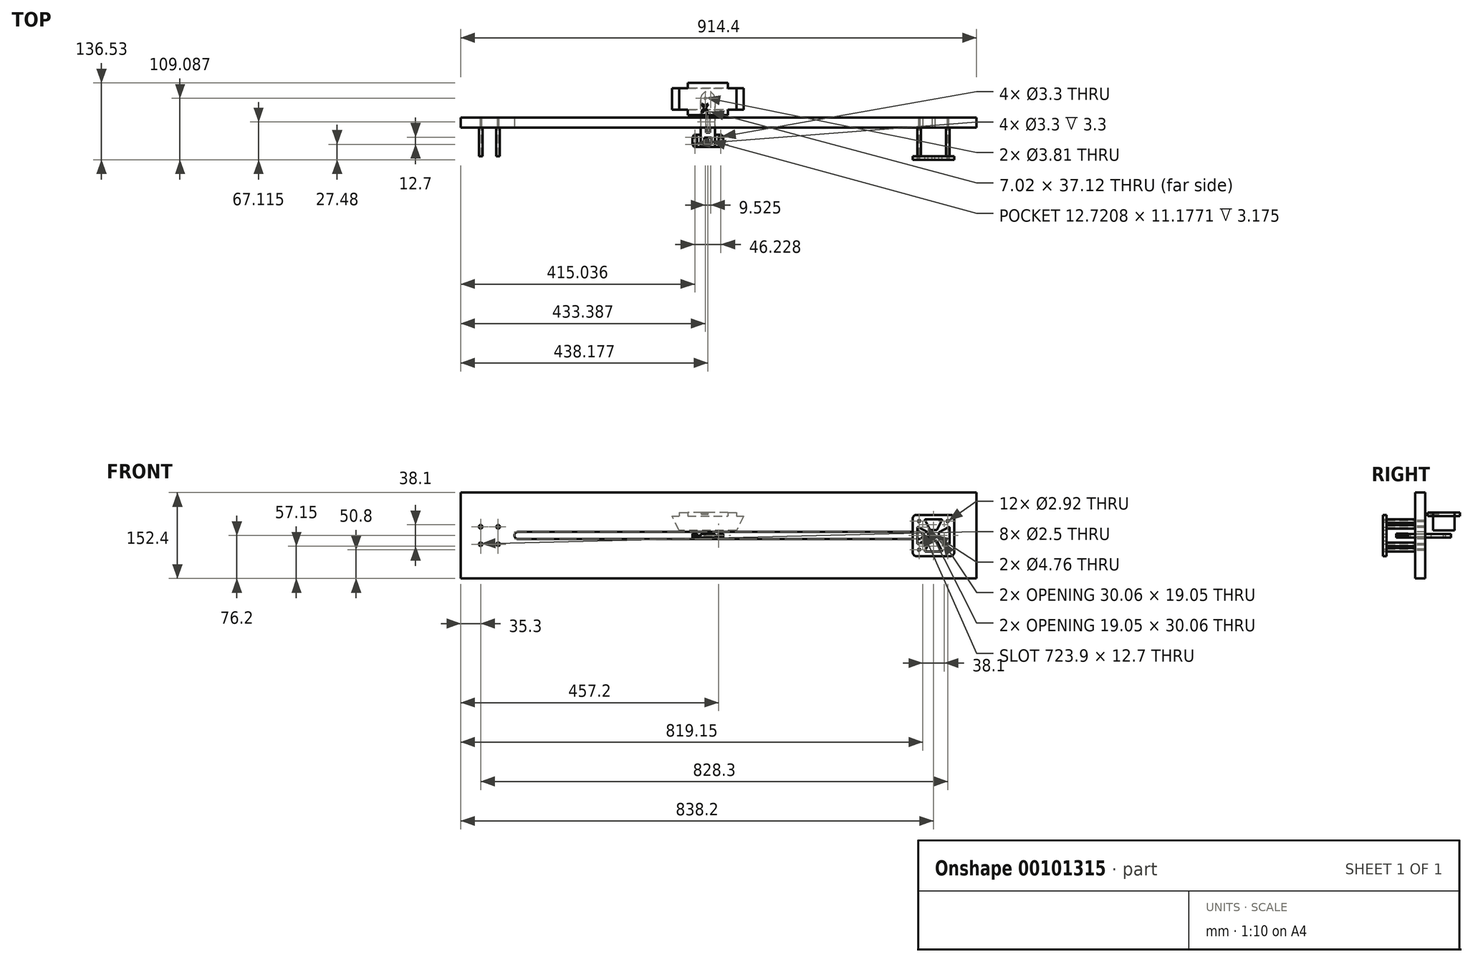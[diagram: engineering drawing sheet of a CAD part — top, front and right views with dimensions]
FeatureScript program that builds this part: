
annotation { "Feature Type Name" : "Feature", "Feature Type Description" : "" }
export const myFeature = defineFeature(function(context is Context, id is Id, definition is map)
    precondition{}
    {
        {
            var Q0;
            Q0=qCreatedBy(makeId("Front.planeOp"),FACE);
            var sketch = newSketch(context, id + "F0", { "sketchPlane" : qUnion([Q0])});
            skLineSegment(sketch, "E0", {"start": v(0, 0) * mm, "end": v(0.2, 0) * mm});
            skArc(sketch, "E1", {"start": v(0.2, 0) * mm, "mid": v(0.29, 0.02) * mm, "end": v(0.34, 0.09) * mm});
            skLineSegment(sketch, "E2", {"start": v(0.75, 0.76) * mm, "end": v(1.25, 0.76) * mm});
            skArc(sketch, "E3", {"start": v(1.66, 0.09) * mm, "mid": v(1.71, 0.02) * mm, "end": v(1.8, 0) * mm});
            skLineSegment(sketch, "E4", {"start": v(1.8, 0) * mm, "end": v(2, 0) * mm});
            skLineSegment(sketch, "E5", {"start": v(0.34, 0.09) * mm, "end": v(0.61, 0.67) * mm});
            skLineSegment(sketch, "E6", {"start": v(1.66, 0.09) * mm, "end": v(1.39, 0.67) * mm});
            skArc(sketch, "E7", {"start": v(1.39, 0.67) * mm, "mid": v(1.33, 0.74) * mm, "end": v(1.25, 0.76) * mm});
            skArc(sketch, "E8", {"start": v(0.61, 0.67) * mm, "mid": v(0.67, 0.74) * mm, "end": v(0.75, 0.76) * mm});
            skLineSegment(sketch, "E9.1.0.0", {"start": v(2, 0) * mm, "end": v(2.2, 0) * mm});
            skArc(sketch, "E9.1.0.1", {"start": v(2.2, 0) * mm, "mid": v(2.29, 0.02) * mm, "end": v(2.34, 0.09) * mm});
            skLineSegment(sketch, "E9.1.0.2", {"start": v(2.34, 0.09) * mm, "end": v(2.61, 0.67) * mm});
            skArc(sketch, "E9.1.0.3", {"start": v(2.61, 0.67) * mm, "mid": v(2.67, 0.74) * mm, "end": v(2.75, 0.76) * mm});
            skLineSegment(sketch, "E9.1.0.4", {"start": v(2.75, 0.76) * mm, "end": v(3.25, 0.76) * mm});
            skArc(sketch, "E9.1.0.5", {"start": v(3.39, 0.67) * mm, "mid": v(3.33, 0.74) * mm, "end": v(3.25, 0.76) * mm});
            skLineSegment(sketch, "E9.1.0.6", {"start": v(3.66, 0.09) * mm, "end": v(3.39, 0.67) * mm});
            skArc(sketch, "E9.1.0.7", {"start": v(3.66, 0.09) * mm, "mid": v(3.71, 0.02) * mm, "end": v(3.8, 0) * mm});
            skLineSegment(sketch, "E9.1.0.8", {"start": v(3.8, 0) * mm, "end": v(4, 0) * mm});
            skLineSegment(sketch, "E9.2.0.0", {"start": v(4, 0) * mm, "end": v(4.2, 0) * mm});
            skArc(sketch, "E9.2.0.1", {"start": v(4.2, 0) * mm, "mid": v(4.29, 0.02) * mm, "end": v(4.34, 0.09) * mm});
            skLineSegment(sketch, "E9.2.0.2", {"start": v(4.34, 0.09) * mm, "end": v(4.61, 0.67) * mm});
            skArc(sketch, "E9.2.0.3", {"start": v(4.61, 0.67) * mm, "mid": v(4.67, 0.74) * mm, "end": v(4.75, 0.76) * mm});
            skLineSegment(sketch, "E9.2.0.4", {"start": v(4.75, 0.76) * mm, "end": v(5.25, 0.76) * mm});
            skArc(sketch, "E9.2.0.5", {"start": v(5.39, 0.67) * mm, "mid": v(5.33, 0.74) * mm, "end": v(5.25, 0.76) * mm});
            skLineSegment(sketch, "E9.2.0.6", {"start": v(5.66, 0.09) * mm, "end": v(5.39, 0.67) * mm});
            skArc(sketch, "E9.2.0.7", {"start": v(5.66, 0.09) * mm, "mid": v(5.71, 0.02) * mm, "end": v(5.8, 0) * mm});
            skLineSegment(sketch, "E9.2.0.8", {"start": v(5.8, 0) * mm, "end": v(6, 0) * mm});
            skLineSegment(sketch, "E9.3.0.0", {"start": v(6, 0) * mm, "end": v(6.2, 0) * mm});
            skArc(sketch, "E9.3.0.1", {"start": v(6.2, 0) * mm, "mid": v(6.29, 0.02) * mm, "end": v(6.34, 0.09) * mm});
            skLineSegment(sketch, "E9.3.0.2", {"start": v(6.34, 0.09) * mm, "end": v(6.61, 0.67) * mm});
            skArc(sketch, "E9.3.0.3", {"start": v(6.61, 0.67) * mm, "mid": v(6.67, 0.74) * mm, "end": v(6.75, 0.76) * mm});
            skLineSegment(sketch, "E9.3.0.4", {"start": v(6.75, 0.76) * mm, "end": v(7.25, 0.76) * mm});
            skArc(sketch, "E9.3.0.5", {"start": v(7.39, 0.67) * mm, "mid": v(7.33, 0.74) * mm, "end": v(7.25, 0.76) * mm});
            skLineSegment(sketch, "E9.3.0.6", {"start": v(7.66, 0.09) * mm, "end": v(7.39, 0.67) * mm});
            skArc(sketch, "E9.3.0.7", {"start": v(7.66, 0.09) * mm, "mid": v(7.71, 0.02) * mm, "end": v(7.8, 0) * mm});
            skLineSegment(sketch, "E9.3.0.8", {"start": v(7.8, 0) * mm, "end": v(8, 0) * mm});
            skLineSegment(sketch, "E9.4.0.0", {"start": v(8, 0) * mm, "end": v(8.2, 0) * mm});
            skArc(sketch, "E9.4.0.1", {"start": v(8.2, 0) * mm, "mid": v(8.29, 0.02) * mm, "end": v(8.34, 0.09) * mm});
            skLineSegment(sketch, "E9.4.0.2", {"start": v(8.34, 0.09) * mm, "end": v(8.61, 0.67) * mm});
            skArc(sketch, "E9.4.0.3", {"start": v(8.61, 0.67) * mm, "mid": v(8.67, 0.74) * mm, "end": v(8.75, 0.76) * mm});
            skLineSegment(sketch, "E9.4.0.4", {"start": v(8.75, 0.76) * mm, "end": v(9.25, 0.76) * mm});
            skArc(sketch, "E9.4.0.5", {"start": v(9.39, 0.67) * mm, "mid": v(9.33, 0.74) * mm, "end": v(9.25, 0.76) * mm});
            skLineSegment(sketch, "E9.4.0.6", {"start": v(9.66, 0.09) * mm, "end": v(9.39, 0.67) * mm});
            skArc(sketch, "E9.4.0.7", {"start": v(9.66, 0.09) * mm, "mid": v(9.71, 0.02) * mm, "end": v(9.8, 0) * mm});
            skLineSegment(sketch, "E9.4.0.8", {"start": v(9.8, 0) * mm, "end": v(10, 0) * mm});
            skLineSegment(sketch, "E9.5.0.0", {"start": v(10, 0) * mm, "end": v(10.2, 0) * mm});
            skArc(sketch, "E9.5.0.1", {"start": v(10.2, 0) * mm, "mid": v(10.29, 0.02) * mm, "end": v(10.34, 0.09) * mm});
            skLineSegment(sketch, "E9.5.0.2", {"start": v(10.34, 0.09) * mm, "end": v(10.61, 0.67) * mm});
            skArc(sketch, "E9.5.0.3", {"start": v(10.61, 0.67) * mm, "mid": v(10.67, 0.74) * mm, "end": v(10.75, 0.76) * mm});
            skLineSegment(sketch, "E9.5.0.4", {"start": v(10.75, 0.76) * mm, "end": v(11.25, 0.76) * mm});
            skArc(sketch, "E9.5.0.5", {"start": v(11.39, 0.67) * mm, "mid": v(11.33, 0.74) * mm, "end": v(11.25, 0.76) * mm});
            skLineSegment(sketch, "E9.5.0.6", {"start": v(11.66, 0.09) * mm, "end": v(11.39, 0.67) * mm});
            skArc(sketch, "E9.5.0.7", {"start": v(11.66, 0.09) * mm, "mid": v(11.71, 0.02) * mm, "end": v(11.8, 0) * mm});
            skLineSegment(sketch, "E9.5.0.8", {"start": v(11.8, 0) * mm, "end": v(12, 0) * mm});
            skLineSegment(sketch, "E9.6.0.0", {"start": v(12, 0) * mm, "end": v(12.2, 0) * mm});
            skArc(sketch, "E9.6.0.1", {"start": v(12.2, 0) * mm, "mid": v(12.29, 0.02) * mm, "end": v(12.34, 0.09) * mm});
            skLineSegment(sketch, "E9.6.0.2", {"start": v(12.34, 0.09) * mm, "end": v(12.61, 0.67) * mm});
            skArc(sketch, "E9.6.0.3", {"start": v(12.61, 0.67) * mm, "mid": v(12.67, 0.74) * mm, "end": v(12.75, 0.76) * mm});
            skLineSegment(sketch, "E9.6.0.4", {"start": v(12.75, 0.76) * mm, "end": v(13.25, 0.76) * mm});
            skArc(sketch, "E9.6.0.5", {"start": v(13.39, 0.67) * mm, "mid": v(13.33, 0.74) * mm, "end": v(13.25, 0.76) * mm});
            skLineSegment(sketch, "E9.6.0.6", {"start": v(13.66, 0.09) * mm, "end": v(13.39, 0.67) * mm});
            skArc(sketch, "E9.6.0.7", {"start": v(13.66, 0.09) * mm, "mid": v(13.71, 0.02) * mm, "end": v(13.8, 0) * mm});
            skLineSegment(sketch, "E9.6.0.8", {"start": v(13.8, 0) * mm, "end": v(14, 0) * mm});
            skLineSegment(sketch, "E9.7.0.0", {"start": v(14, 0) * mm, "end": v(14.2, 0) * mm});
            skArc(sketch, "E9.7.0.1", {"start": v(14.2, 0) * mm, "mid": v(14.29, 0.02) * mm, "end": v(14.34, 0.09) * mm});
            skLineSegment(sketch, "E9.7.0.2", {"start": v(14.34, 0.09) * mm, "end": v(14.61, 0.67) * mm});
            skArc(sketch, "E9.7.0.3", {"start": v(14.61, 0.67) * mm, "mid": v(14.67, 0.74) * mm, "end": v(14.75, 0.76) * mm});
            skLineSegment(sketch, "E9.7.0.4", {"start": v(14.75, 0.76) * mm, "end": v(15.25, 0.76) * mm});
            skArc(sketch, "E9.7.0.5", {"start": v(15.39, 0.67) * mm, "mid": v(15.33, 0.74) * mm, "end": v(15.25, 0.76) * mm});
            skLineSegment(sketch, "E9.7.0.6", {"start": v(15.66, 0.09) * mm, "end": v(15.39, 0.67) * mm});
            skArc(sketch, "E9.7.0.7", {"start": v(15.66, 0.09) * mm, "mid": v(15.71, 0.02) * mm, "end": v(15.8, 0) * mm});
            skLineSegment(sketch, "E9.7.0.8", {"start": v(15.8, 0) * mm, "end": v(16, 0) * mm});
            skLineSegment(sketch, "E9.direction1", {"start": v(0, 0) * mm, "end": v(2, 0) * mm, "construction": true});
            skLineSegment(sketch, "E10", {"start": v(0, 0) * mm, "end": v(0, -0.76) * mm});
            skLineSegment(sketch, "E11", {"start": v(0, -0.76) * mm, "end": v(16, -0.76) * mm});
            skLineSegment(sketch, "E12", {"start": v(16, -0.76) * mm, "end": v(16, 0) * mm});
            skSolve(sketch);
        }
        {
            var Q0;
            Q0=makeQuery(id+"F0.imprint","IMPRINT",FACE,{"disambiguationData":[TD([[makeQuery(id+"F0.imprint","IMPRINT",EDGE,{"derivedFrom":sQuery(id+"F0.wireOp",EDGE,"E0")}),-1.0]])]});
            extrude(context, id + "F1", {"entities" : qUnion([Q0]), "depth" : 6 * mm});
        }
        {
            var Q0;
            Q0=makeQuery(id+"F1.opExtrude","CAP_FACE",FACE,{"disambiguationData":[OSD([sQuery(id+"F0.wireOp",EDGE,"E0"),sQuery(id+"F0.wireOp",EDGE,"E1"),sQuery(id+"F0.wireOp",EDGE,"E2"),sQuery(id+"F0.wireOp",EDGE,"E3"),sQuery(id+"F0.wireOp",EDGE,"E4"),sQuery(id+"F0.wireOp",EDGE,"E5"),sQuery(id+"F0.wireOp",EDGE,"E6"),sQuery(id+"F0.wireOp",EDGE,"E7"),sQuery(id+"F0.wireOp",EDGE,"E8"),sQuery(id+"F0.wireOp",EDGE,"E9.1.0.0"),sQuery(id+"F0.wireOp",EDGE,"E9.1.0.1"),sQuery(id+"F0.wireOp",EDGE,"E9.1.0.2"),sQuery(id+"F0.wireOp",EDGE,"E9.1.0.3"),sQuery(id+"F0.wireOp",EDGE,"E9.1.0.4"),sQuery(id+"F0.wireOp",EDGE,"E9.1.0.5"),sQuery(id+"F0.wireOp",EDGE,"E9.1.0.6"),sQuery(id+"F0.wireOp",EDGE,"E9.1.0.7"),sQuery(id+"F0.wireOp",EDGE,"E9.1.0.8"),sQuery(id+"F0.wireOp",EDGE,"E9.2.0.0"),sQuery(id+"F0.wireOp",EDGE,"E9.2.0.1"),sQuery(id+"F0.wireOp",EDGE,"E9.2.0.2"),sQuery(id+"F0.wireOp",EDGE,"E9.2.0.3"),sQuery(id+"F0.wireOp",EDGE,"E9.2.0.4"),sQuery(id+"F0.wireOp",EDGE,"E9.2.0.5"),sQuery(id+"F0.wireOp",EDGE,"E9.2.0.6"),sQuery(id+"F0.wireOp",EDGE,"E9.2.0.7"),sQuery(id+"F0.wireOp",EDGE,"E9.2.0.8"),sQuery(id+"F0.wireOp",EDGE,"E9.3.0.0"),sQuery(id+"F0.wireOp",EDGE,"E9.3.0.1"),sQuery(id+"F0.wireOp",EDGE,"E9.3.0.2"),sQuery(id+"F0.wireOp",EDGE,"E9.3.0.3"),sQuery(id+"F0.wireOp",EDGE,"E9.3.0.4"),sQuery(id+"F0.wireOp",EDGE,"E9.3.0.5"),sQuery(id+"F0.wireOp",EDGE,"E9.3.0.6"),sQuery(id+"F0.wireOp",EDGE,"E9.3.0.7"),sQuery(id+"F0.wireOp",EDGE,"E9.3.0.8"),sQuery(id+"F0.wireOp",EDGE,"E9.4.0.0"),sQuery(id+"F0.wireOp",EDGE,"E9.4.0.1"),sQuery(id+"F0.wireOp",EDGE,"E9.4.0.2"),sQuery(id+"F0.wireOp",EDGE,"E9.4.0.3"),sQuery(id+"F0.wireOp",EDGE,"E9.4.0.4"),sQuery(id+"F0.wireOp",EDGE,"E9.4.0.5"),sQuery(id+"F0.wireOp",EDGE,"E9.4.0.6"),sQuery(id+"F0.wireOp",EDGE,"E9.4.0.7"),sQuery(id+"F0.wireOp",EDGE,"E9.4.0.8"),sQuery(id+"F0.wireOp",EDGE,"E9.5.0.0"),sQuery(id+"F0.wireOp",EDGE,"E9.5.0.1"),sQuery(id+"F0.wireOp",EDGE,"E9.5.0.2"),sQuery(id+"F0.wireOp",EDGE,"E9.5.0.3"),sQuery(id+"F0.wireOp",EDGE,"E9.5.0.4"),sQuery(id+"F0.wireOp",EDGE,"E9.5.0.5"),sQuery(id+"F0.wireOp",EDGE,"E9.5.0.6"),sQuery(id+"F0.wireOp",EDGE,"E9.5.0.7"),sQuery(id+"F0.wireOp",EDGE,"E9.5.0.8"),sQuery(id+"F0.wireOp",EDGE,"E9.6.0.0"),sQuery(id+"F0.wireOp",EDGE,"E9.6.0.1"),sQuery(id+"F0.wireOp",EDGE,"E9.6.0.2"),sQuery(id+"F0.wireOp",EDGE,"E9.6.0.3"),sQuery(id+"F0.wireOp",EDGE,"E9.6.0.4"),sQuery(id+"F0.wireOp",EDGE,"E9.6.0.5"),sQuery(id+"F0.wireOp",EDGE,"E9.6.0.6"),sQuery(id+"F0.wireOp",EDGE,"E9.6.0.7"),sQuery(id+"F0.wireOp",EDGE,"E9.6.0.8"),sQuery(id+"F0.wireOp",EDGE,"E9.7.0.0"),sQuery(id+"F0.wireOp",EDGE,"E9.7.0.1"),sQuery(id+"F0.wireOp",EDGE,"E9.7.0.2"),sQuery(id+"F0.wireOp",EDGE,"E9.7.0.3"),sQuery(id+"F0.wireOp",EDGE,"E9.7.0.4"),sQuery(id+"F0.wireOp",EDGE,"E9.7.0.5"),sQuery(id+"F0.wireOp",EDGE,"E9.7.0.6"),sQuery(id+"F0.wireOp",EDGE,"E9.7.0.7"),sQuery(id+"F0.wireOp",EDGE,"E9.7.0.8"),sQuery(id+"F0.wireOp",EDGE,"E10"),sQuery(id+"F0.wireOp",EDGE,"E11"),sQuery(id+"F0.wireOp",EDGE,"E12")])],"isStart":false});
            var sketch = newSketch(context, id + "F2", { "sketchPlane" : qUnion([Q0])});
            skLineSegment(sketch, "E13.bottom", {"start": v(0, -3.94) * mm, "end": v(8, -3.94) * mm});
            skLineSegment(sketch, "E13.top", {"start": v(0, 3.3) * mm, "end": v(8, 3.3) * mm});
            skLineSegment(sketch, "E13.left", {"start": v(0, -3.94) * mm, "end": v(0, 3.3) * mm});
            skLineSegment(sketch, "E13.right", {"start": v(8, -3.94) * mm, "end": v(8, 3.3) * mm});
            skPoint(sketch, "E14", {"position": v(8, 0) * mm});
            skSolve(sketch);
        }
        {
            var Q0;
            Q0 = qSketchRegion(id + "F2", true);
            extrude(context, id + "F3", {"entities" : qUnion([Q0]), "oppositeDirection" : true, "depth" : 6 * mm});
        }
        {
            var Q0;
            Q0=makeQuery(id+"F1.opExtrude","SWEPT_BODY",BODY,{"disambiguationData":[OSD([sQuery(id+"F0.wireOp",EDGE,"E0"),sQuery(id+"F0.wireOp",EDGE,"E1"),sQuery(id+"F0.wireOp",EDGE,"E2"),sQuery(id+"F0.wireOp",EDGE,"E3"),sQuery(id+"F0.wireOp",EDGE,"E4"),sQuery(id+"F0.wireOp",EDGE,"E5"),sQuery(id+"F0.wireOp",EDGE,"E6"),sQuery(id+"F0.wireOp",EDGE,"E7"),sQuery(id+"F0.wireOp",EDGE,"E8"),sQuery(id+"F0.wireOp",EDGE,"E9.1.0.0"),sQuery(id+"F0.wireOp",EDGE,"E9.1.0.1"),sQuery(id+"F0.wireOp",EDGE,"E9.1.0.2"),sQuery(id+"F0.wireOp",EDGE,"E9.1.0.3"),sQuery(id+"F0.wireOp",EDGE,"E9.1.0.4"),sQuery(id+"F0.wireOp",EDGE,"E9.1.0.5"),sQuery(id+"F0.wireOp",EDGE,"E9.1.0.6"),sQuery(id+"F0.wireOp",EDGE,"E9.1.0.7"),sQuery(id+"F0.wireOp",EDGE,"E9.1.0.8"),sQuery(id+"F0.wireOp",EDGE,"E9.2.0.0"),sQuery(id+"F0.wireOp",EDGE,"E9.2.0.1"),sQuery(id+"F0.wireOp",EDGE,"E9.2.0.2"),sQuery(id+"F0.wireOp",EDGE,"E9.2.0.3"),sQuery(id+"F0.wireOp",EDGE,"E9.2.0.4"),sQuery(id+"F0.wireOp",EDGE,"E9.2.0.5"),sQuery(id+"F0.wireOp",EDGE,"E9.2.0.6"),sQuery(id+"F0.wireOp",EDGE,"E9.2.0.7"),sQuery(id+"F0.wireOp",EDGE,"E9.2.0.8"),sQuery(id+"F0.wireOp",EDGE,"E9.3.0.0"),sQuery(id+"F0.wireOp",EDGE,"E9.3.0.1"),sQuery(id+"F0.wireOp",EDGE,"E9.3.0.2"),sQuery(id+"F0.wireOp",EDGE,"E9.3.0.3"),sQuery(id+"F0.wireOp",EDGE,"E9.3.0.4"),sQuery(id+"F0.wireOp",EDGE,"E9.3.0.5"),sQuery(id+"F0.wireOp",EDGE,"E9.3.0.6"),sQuery(id+"F0.wireOp",EDGE,"E9.3.0.7"),sQuery(id+"F0.wireOp",EDGE,"E9.3.0.8"),sQuery(id+"F0.wireOp",EDGE,"E9.4.0.0"),sQuery(id+"F0.wireOp",EDGE,"E9.4.0.1"),sQuery(id+"F0.wireOp",EDGE,"E9.4.0.2"),sQuery(id+"F0.wireOp",EDGE,"E9.4.0.3"),sQuery(id+"F0.wireOp",EDGE,"E9.4.0.4"),sQuery(id+"F0.wireOp",EDGE,"E9.4.0.5"),sQuery(id+"F0.wireOp",EDGE,"E9.4.0.6"),sQuery(id+"F0.wireOp",EDGE,"E9.4.0.7"),sQuery(id+"F0.wireOp",EDGE,"E9.4.0.8"),sQuery(id+"F0.wireOp",EDGE,"E9.5.0.0"),sQuery(id+"F0.wireOp",EDGE,"E9.5.0.1"),sQuery(id+"F0.wireOp",EDGE,"E9.5.0.2"),sQuery(id+"F0.wireOp",EDGE,"E9.5.0.3"),sQuery(id+"F0.wireOp",EDGE,"E9.5.0.4"),sQuery(id+"F0.wireOp",EDGE,"E9.5.0.5"),sQuery(id+"F0.wireOp",EDGE,"E9.5.0.6"),sQuery(id+"F0.wireOp",EDGE,"E9.5.0.7"),sQuery(id+"F0.wireOp",EDGE,"E9.5.0.8"),sQuery(id+"F0.wireOp",EDGE,"E9.6.0.0"),sQuery(id+"F0.wireOp",EDGE,"E9.6.0.1"),sQuery(id+"F0.wireOp",EDGE,"E9.6.0.2"),sQuery(id+"F0.wireOp",EDGE,"E9.6.0.3"),sQuery(id+"F0.wireOp",EDGE,"E9.6.0.4"),sQuery(id+"F0.wireOp",EDGE,"E9.6.0.5"),sQuery(id+"F0.wireOp",EDGE,"E9.6.0.6"),sQuery(id+"F0.wireOp",EDGE,"E9.6.0.7"),sQuery(id+"F0.wireOp",EDGE,"E9.6.0.8"),sQuery(id+"F0.wireOp",EDGE,"E9.7.0.0"),sQuery(id+"F0.wireOp",EDGE,"E9.7.0.1"),sQuery(id+"F0.wireOp",EDGE,"E9.7.0.2"),sQuery(id+"F0.wireOp",EDGE,"E9.7.0.3"),sQuery(id+"F0.wireOp",EDGE,"E9.7.0.4"),sQuery(id+"F0.wireOp",EDGE,"E9.7.0.5"),sQuery(id+"F0.wireOp",EDGE,"E9.7.0.6"),sQuery(id+"F0.wireOp",EDGE,"E9.7.0.7"),sQuery(id+"F0.wireOp",EDGE,"E9.7.0.8"),sQuery(id+"F0.wireOp",EDGE,"E10"),sQuery(id+"F0.wireOp",EDGE,"E11"),sQuery(id+"F0.wireOp",EDGE,"E12")])]});
            var Q1;
            Q1=makeQuery(id+"F3.opExtrude","SWEPT_BODY",BODY,{"disambiguationData":[OSD([sQuery(id+"F2.wireOp",EDGE,"E13.bottom"),sQuery(id+"F2.wireOp",EDGE,"E13.top"),sQuery(id+"F2.wireOp",EDGE,"E13.left"),sQuery(id+"F2.wireOp",EDGE,"E13.right")])]});
            booleanBodies(context, id + "F4", {"operationType" : BooleanOperationType.SUBTRACTION, "tools" : qUnion([Q0]), "targets" : qUnion([Q1])});
        }
        {
            var Q0;
            {var subQ0=sQuery(id+"F2.wireOp",EDGE,"E13.top");var subQ1=sQuery(id+"F2.wireOp",EDGE,"E13.left");var subQ2=sQuery(id+"F2.wireOp",EDGE,"E13.right");Q0=makeQuery(id+"F4.opBoolean","SPLIT",FACE,{"disambiguationData":[TD([makeQuery(id+"F1.opExtrude","SWEPT_FACE",FACE,{"disambiguationData":[OSD([sQuery(id+"F0.wireOp",EDGE,"E0")])]})])],"derivedFrom":makeQuery(id+"F3.opExtrude","CAP_FACE",FACE,{"disambiguationData":[OSD([sQuery(id+"F2.wireOp",EDGE,"E13.bottom"),subQ0,subQ1,subQ2])],"isStart":false})});}
            var sketch = newSketch(context, id + "F5", { "sketchPlane" : qUnion([Q0])});
            skSolve(sketch);
        }
        {
            var Q0;
            {var subQ2=sQuery(id+"F2.wireOp",EDGE,"E13.top");Q0=makeQuery(id+"F5.imprint","IMPRINT",FACE,{"disambiguationData":[TD([[makeQuery(id+"F5.imprint","IMPRINT",EDGE,{"derivedFrom":makeQuery(id+"F3.opExtrude","CAP_EDGE",EDGE,{"disambiguationData":[OSD([subQ2])],"isStart":false})}),1.0]])]});}
            extrude(context, id + "F6", {"entities" : qUnion([Q0]), "operationType" : NewBodyOperationType.ADD, "depth" : 7.62 * mm});
        }
        {
            var Q0;
            {var subQ0=sQuery(id+"F2.wireOp",EDGE,"E13.top");var subQ1=sQuery(id+"F2.wireOp",EDGE,"E13.left");var subQ2=sQuery(id+"F2.wireOp",EDGE,"E13.right");Q0=makeQuery(id+"F4.opBoolean","SPLIT",FACE,{"disambiguationData":[TD([makeQuery(id+"F1.opExtrude","SWEPT_FACE",FACE,{"disambiguationData":[OSD([sQuery(id+"F0.wireOp",EDGE,"E0")])]})])],"derivedFrom":makeQuery(id+"F3.opExtrude","CAP_FACE",FACE,{"disambiguationData":[OSD([sQuery(id+"F2.wireOp",EDGE,"E13.bottom"),subQ0,subQ1,subQ2])],"isStart":true})});}
            var sketch = newSketch(context, id + "F7", { "sketchPlane" : qUnion([Q0])});
            skSolve(sketch);
        }
        {
            var Q0;
            {var subQ1=sQuery(id+"F2.wireOp",EDGE,"E13.top");Q0=makeQuery(id+"F7.imprint","IMPRINT",FACE,{"disambiguationData":[TD([[makeQuery(id+"F7.imprint","IMPRINT",EDGE,{"derivedFrom":makeQuery(id+"F3.opExtrude","CAP_EDGE",EDGE,{"disambiguationData":[OSD([subQ1])],"isStart":true})}),-1.0]])]});}
            extrude(context, id + "F8", {"entities" : qUnion([Q0]), "operationType" : NewBodyOperationType.ADD, "depth" : 7.62 * mm});
        }
        {
            var Q0;
            {var subQ0=sQuery(id+"F2.wireOp",EDGE,"E13.left");var subQ1=sQuery(id+"F2.wireOp",EDGE,"E13.right");var subQ2=sQuery(id+"F2.wireOp",EDGE,"E13.bottom");Q0=makeQuery(id+"F4.opBoolean","SPLIT",FACE,{"disambiguationData":[TD([makeQuery(id+"F1.opExtrude","SWEPT_FACE",FACE,{"disambiguationData":[OSD([sQuery(id+"F0.wireOp",EDGE,"E11")])]})])],"derivedFrom":makeQuery(id+"F3.opExtrude","CAP_FACE",FACE,{"disambiguationData":[OSD([subQ2,sQuery(id+"F2.wireOp",EDGE,"E13.top"),subQ0,subQ1])],"isStart":false})});}
            var sketch = newSketch(context, id + "F9", { "sketchPlane" : qUnion([Q0])});
            skSolve(sketch);
        }
        {
            var Q0;
            {var subQ0=sQuery(id+"F2.wireOp",EDGE,"E13.bottom");Q0=makeQuery(id+"F9.imprint","IMPRINT",FACE,{"disambiguationData":[TD([[makeQuery(id+"F9.imprint","IMPRINT",EDGE,{"derivedFrom":makeQuery(id+"F3.opExtrude","CAP_EDGE",EDGE,{"disambiguationData":[OSD([subQ0])],"isStart":false})}),-1.0]])]});}
            var Q1;
            Q1=makeQuery(id+"F6.opExtrude","CAP_FACE",FACE,{"disambiguationData":[OSD([sQuery(id+"F0.wireOp",EDGE,"E0"),sQuery(id+"F0.wireOp",EDGE,"E1"),sQuery(id+"F0.wireOp",EDGE,"E2"),sQuery(id+"F0.wireOp",EDGE,"E3"),sQuery(id+"F0.wireOp",EDGE,"E4"),sQuery(id+"F0.wireOp",EDGE,"E5"),sQuery(id+"F0.wireOp",EDGE,"E6"),sQuery(id+"F0.wireOp",EDGE,"E7"),sQuery(id+"F0.wireOp",EDGE,"E8"),sQuery(id+"F0.wireOp",EDGE,"E9.1.0.0"),sQuery(id+"F0.wireOp",EDGE,"E9.1.0.1"),sQuery(id+"F0.wireOp",EDGE,"E9.1.0.2"),sQuery(id+"F0.wireOp",EDGE,"E9.1.0.3"),sQuery(id+"F0.wireOp",EDGE,"E9.1.0.4"),sQuery(id+"F0.wireOp",EDGE,"E9.1.0.5"),sQuery(id+"F0.wireOp",EDGE,"E9.1.0.6"),sQuery(id+"F0.wireOp",EDGE,"E9.1.0.7"),sQuery(id+"F0.wireOp",EDGE,"E9.1.0.8"),sQuery(id+"F0.wireOp",EDGE,"E9.2.0.0"),sQuery(id+"F0.wireOp",EDGE,"E9.2.0.1"),sQuery(id+"F0.wireOp",EDGE,"E9.2.0.2"),sQuery(id+"F0.wireOp",EDGE,"E9.2.0.3"),sQuery(id+"F0.wireOp",EDGE,"E9.2.0.4"),sQuery(id+"F0.wireOp",EDGE,"E9.2.0.5"),sQuery(id+"F0.wireOp",EDGE,"E9.2.0.6"),sQuery(id+"F0.wireOp",EDGE,"E9.2.0.7"),sQuery(id+"F0.wireOp",EDGE,"E9.2.0.8"),sQuery(id+"F0.wireOp",EDGE,"E9.3.0.0"),sQuery(id+"F0.wireOp",EDGE,"E9.3.0.1"),sQuery(id+"F0.wireOp",EDGE,"E9.3.0.2"),sQuery(id+"F0.wireOp",EDGE,"E9.3.0.3"),sQuery(id+"F0.wireOp",EDGE,"E9.3.0.4"),sQuery(id+"F0.wireOp",EDGE,"E9.3.0.5"),sQuery(id+"F0.wireOp",EDGE,"E9.3.0.6"),sQuery(id+"F0.wireOp",EDGE,"E9.3.0.7"),sQuery(id+"F0.wireOp",EDGE,"E9.3.0.8"),sQuery(id+"F0.wireOp",EDGE,"E9.4.0.0"),sQuery(id+"F2.wireOp",EDGE,"E13.top"),sQuery(id+"F2.wireOp",EDGE,"E13.left"),sQuery(id+"F2.wireOp",EDGE,"E13.right")])],"isStart":false});
            var Q2;
            Q2=makeQuery(id+"F8.opExtrude","CAP_FACE",FACE,{"disambiguationData":[OSD([sQuery(id+"F0.wireOp",EDGE,"E0"),sQuery(id+"F0.wireOp",EDGE,"E1"),sQuery(id+"F0.wireOp",EDGE,"E2"),sQuery(id+"F0.wireOp",EDGE,"E3"),sQuery(id+"F0.wireOp",EDGE,"E4"),sQuery(id+"F0.wireOp",EDGE,"E5"),sQuery(id+"F0.wireOp",EDGE,"E6"),sQuery(id+"F0.wireOp",EDGE,"E7"),sQuery(id+"F0.wireOp",EDGE,"E8"),sQuery(id+"F0.wireOp",EDGE,"E9.1.0.0"),sQuery(id+"F0.wireOp",EDGE,"E9.1.0.1"),sQuery(id+"F0.wireOp",EDGE,"E9.1.0.2"),sQuery(id+"F0.wireOp",EDGE,"E9.1.0.3"),sQuery(id+"F0.wireOp",EDGE,"E9.1.0.4"),sQuery(id+"F0.wireOp",EDGE,"E9.1.0.5"),sQuery(id+"F0.wireOp",EDGE,"E9.1.0.6"),sQuery(id+"F0.wireOp",EDGE,"E9.1.0.7"),sQuery(id+"F0.wireOp",EDGE,"E9.1.0.8"),sQuery(id+"F0.wireOp",EDGE,"E9.2.0.0"),sQuery(id+"F0.wireOp",EDGE,"E9.2.0.1"),sQuery(id+"F0.wireOp",EDGE,"E9.2.0.2"),sQuery(id+"F0.wireOp",EDGE,"E9.2.0.3"),sQuery(id+"F0.wireOp",EDGE,"E9.2.0.4"),sQuery(id+"F0.wireOp",EDGE,"E9.2.0.5"),sQuery(id+"F0.wireOp",EDGE,"E9.2.0.6"),sQuery(id+"F0.wireOp",EDGE,"E9.2.0.7"),sQuery(id+"F0.wireOp",EDGE,"E9.2.0.8"),sQuery(id+"F0.wireOp",EDGE,"E9.3.0.0"),sQuery(id+"F0.wireOp",EDGE,"E9.3.0.1"),sQuery(id+"F0.wireOp",EDGE,"E9.3.0.2"),sQuery(id+"F0.wireOp",EDGE,"E9.3.0.3"),sQuery(id+"F0.wireOp",EDGE,"E9.3.0.4"),sQuery(id+"F0.wireOp",EDGE,"E9.3.0.5"),sQuery(id+"F0.wireOp",EDGE,"E9.3.0.6"),sQuery(id+"F0.wireOp",EDGE,"E9.3.0.7"),sQuery(id+"F0.wireOp",EDGE,"E9.3.0.8"),sQuery(id+"F0.wireOp",EDGE,"E9.4.0.0"),sQuery(id+"F2.wireOp",EDGE,"E13.top"),sQuery(id+"F2.wireOp",EDGE,"E13.left"),sQuery(id+"F2.wireOp",EDGE,"E13.right")])],"isStart":false});
            extrude(context, id + "F10", {"entities" : qUnion([Q0]), "operationType" : NewBodyOperationType.ADD, "endBound" : BoundingType.UP_TO_SURFACE, "endBoundEntityFace" : qUnion([Q1]), "depth" : 25.4 * mm, "hasSecondDirection" : true, "secondDirectionBound" : SecondDirectionBoundingType.UP_TO_SURFACE, "secondDirectionOppositeDirection" : true, "secondDirectionBoundEntityFace" : qUnion([Q2]), "secondDirectionDepth" : 25.4 * mm});
        }
        {
            var Q0;
            {var subQ0=sQuery(id+"F2.wireOp",EDGE,"E13.top");Q0=makeQuery(id+"F8.boolean.opBoolean","MERGE",FACE,{"derivedFrom":[makeQuery(id+"F6.boolean.opBoolean","MERGE",FACE,{"derivedFrom":[makeQuery(id+"F3.opExtrude","SWEPT_FACE",FACE,{"disambiguationData":[OSD([subQ0])]}),makeQuery(id+"F6.opExtrude","SWEPT_FACE",FACE,{"disambiguationData":[OSD([subQ0])]})]}),makeQuery(id+"F8.opExtrude","SWEPT_FACE",FACE,{"disambiguationData":[OSD([subQ0])]})]});}
            var sketch = newSketch(context, id + "F11", { "sketchPlane" : qUnion([Q0])});
            skLineSegment(sketch, "E15", {"start": v(8, -8.54) * mm, "end": v(5.59, -13.62) * mm});
            skLineSegment(sketch, "E16", {"start": v(5.59, -13.62) * mm, "end": v(8, -13.62) * mm});
            skLineSegment(sketch, "E17", {"start": v(8, -13.62) * mm, "end": v(8, -8.54) * mm});
            skLineSegment(sketch, "E18", {"start": v(2.41, -13.62) * mm, "end": v(0, -13.62) * mm});
            skLineSegment(sketch, "E19", {"start": v(0, -13.62) * mm, "end": v(0, -8.54) * mm});
            skLineSegment(sketch, "E20", {"start": v(0, -8.54) * mm, "end": v(2.41, -13.62) * mm});
            skLineSegment(sketch, "E21", {"start": v(8, 2.54) * mm, "end": v(5.59, 7.62) * mm});
            skLineSegment(sketch, "E22", {"start": v(5.59, 7.62) * mm, "end": v(8, 7.62) * mm});
            skLineSegment(sketch, "E23", {"start": v(8, 7.62) * mm, "end": v(8, 2.54) * mm});
            skLineSegment(sketch, "E24", {"start": v(0, 2.54) * mm, "end": v(0, 7.62) * mm});
            skLineSegment(sketch, "E25", {"start": v(0, 7.62) * mm, "end": v(2.41, 7.62) * mm});
            skLineSegment(sketch, "E26", {"start": v(2.41, 7.62) * mm, "end": v(0, 2.54) * mm});
            skSolve(sketch);
        }
        {
            var Q0;
            Q0 = qSketchRegion(id + "F11", true);
            extrude(context, id + "F12", {"entities" : qUnion([Q0]), "operationType" : NewBodyOperationType.REMOVE, "endBound" : BoundingType.THROUGH_ALL, "oppositeDirection" : true, "depth" : 25.4 * mm});
        }
        {
            var Q0;
            {var subQ0=sQuery(id+"F2.wireOp",EDGE,"E13.left");Q0=makeQuery(id+"F10.boolean.opBoolean","MERGE",FACE,{"derivedFrom":[makeQuery(id+"F4.opBoolean","SPLIT",FACE,{"disambiguationData":[TD([makeQuery(id+"F1.opExtrude","SWEPT_FACE",FACE,{"disambiguationData":[OSD([sQuery(id+"F0.wireOp",EDGE,"E11")])]})])],"derivedFrom":makeQuery(id+"F3.opExtrude","SWEPT_FACE",FACE,{"disambiguationData":[OSD([subQ0])]})}),makeQuery(id+"F10.opExtrude","SWEPT_FACE",FACE,{"disambiguationData":[OSD([subQ0])]})]});}
            var sketch = newSketch(context, id + "F13", { "sketchPlane" : qUnion([Q0])});
            skLineSegment(sketch, "E27.0", {"start": v(-7.62, -3.94) * mm, "end": v(-7.62, -0.76) * mm});
            skLineSegment(sketch, "E28.0", {"start": v(-7.62, -0.76) * mm, "end": v(-2.54, -0.76) * mm});
            skLineSegment(sketch, "E29.0", {"start": v(-2.54, -3.94) * mm, "end": v(-7.62, -3.94) * mm});
            skLineSegment(sketch, "E30.0", {"start": v(-2.54, -3.94) * mm, "end": v(8.54, -3.94) * mm});
            skLineSegment(sketch, "E31.0", {"start": v(8.54, -0.76) * mm, "end": v(-2.54, -0.76) * mm});
            skLineSegment(sketch, "E32.0", {"start": v(8.54, -0.76) * mm, "end": v(13.62, -0.76) * mm});
            skLineSegment(sketch, "E33.0", {"start": v(13.62, -3.94) * mm, "end": v(13.62, -0.76) * mm});
            skLineSegment(sketch, "E34.0", {"start": v(13.62, -3.94) * mm, "end": v(8.54, -3.94) * mm});
            skSolve(sketch);
        }
        {
            var Q0;
            Q0 = qSketchRegion(id + "F13", true);
            extrude(context, id + "F14", {"entities" : qUnion([Q0]), "operationType" : NewBodyOperationType.ADD, "depth" : 19.05 * mm, "hasSecondDirection" : true, "secondDirectionOppositeDirection" : true, "secondDirectionDepth" : 3.8 * mm});
        }
        {
            var Q0;
            Q0=makeQuery(id+"F4.opBoolean","SPLIT",BODY,{"disambiguationData":[OD(0.0)],"derivedFrom":makeQuery(id+"F3.opExtrude","SWEPT_BODY",BODY,{"disambiguationData":[OSD([sQuery(id+"F2.wireOp",EDGE,"E13.bottom"),sQuery(id+"F2.wireOp",EDGE,"E13.top"),sQuery(id+"F2.wireOp",EDGE,"E13.left"),sQuery(id+"F2.wireOp",EDGE,"E13.right")])]})});
            var Q1;
            Q1=makeQuery(id+"F4.opBoolean","SPLIT",BODY,{"disambiguationData":[OD(1.0)],"derivedFrom":makeQuery(id+"F3.opExtrude","SWEPT_BODY",BODY,{"disambiguationData":[OSD([sQuery(id+"F2.wireOp",EDGE,"E13.bottom"),sQuery(id+"F2.wireOp",EDGE,"E13.top"),sQuery(id+"F2.wireOp",EDGE,"E13.left"),sQuery(id+"F2.wireOp",EDGE,"E13.right")])]})});
            var Q2;
            Q2=makeQuery(id+"F14.opExtrude","CAP_FACE",FACE,{"disambiguationData":[OSD([sQuery(id+"F13.wireOp",EDGE,"E27.0"),sQuery(id+"F13.wireOp",EDGE,"E28.0"),sQuery(id+"F13.wireOp",EDGE,"E29.0"),sQuery(id+"F13.wireOp",EDGE,"E30.0"),sQuery(id+"F13.wireOp",EDGE,"E31.0"),sQuery(id+"F13.wireOp",EDGE,"E32.0"),sQuery(id+"F13.wireOp",EDGE,"E33.0"),sQuery(id+"F13.wireOp",EDGE,"E34.0")])],"isStart":false});
            mirror(context, id + "F15", {"operationType" : NewBodyOperationType.ADD, "entities" : qUnion([Q0, Q1]), "mirrorPlane" : qUnion([Q2])});
        }
        {
            var Q0;
            {var subQ0=sQuery(id+"F2.wireOp",EDGE,"E13.top");Q0=makeQuery(id+"F15.opPattern","COPY",FACE,{"derivedFrom":makeQuery(id+"F8.boolean.opBoolean","MERGE",FACE,{"derivedFrom":[makeQuery(id+"F6.boolean.opBoolean","MERGE",FACE,{"derivedFrom":[makeQuery(id+"F3.opExtrude","SWEPT_FACE",FACE,{"disambiguationData":[OSD([subQ0])]}),makeQuery(id+"F6.opExtrude","SWEPT_FACE",FACE,{"disambiguationData":[OSD([subQ0])]})]}),makeQuery(id+"F8.opExtrude","SWEPT_FACE",FACE,{"disambiguationData":[OSD([subQ0])]})]}),"instanceName":"1"});}
            var sketch = newSketch(context, id + "F16", { "sketchPlane" : qUnion([Q0])});
            skCircle(sketch, "E35", {"center": v(-42.16, 3.35) * mm, "radius": 1.65 * mm});
            skCircle(sketch, "E36", {"center": v(-42.16, -9.35) * mm, "radius": 1.65 * mm});
            skCircle(sketch, "E37", {"center": v(4.06, 3.35) * mm, "radius": 1.65 * mm});
            skCircle(sketch, "E38", {"center": v(4.06, -9.35) * mm, "radius": 1.65 * mm});
            skLineSegment(sketch, "E39.bottom", {"start": v(4.06, -9.35) * mm, "end": v(-42.16, -9.35) * mm});
            skLineSegment(sketch, "E39.top", {"start": v(4.06, 3.35) * mm, "end": v(-42.16, 3.35) * mm});
            skLineSegment(sketch, "E39.left", {"start": v(4.06, -9.35) * mm, "end": v(4.06, 3.35) * mm});
            skLineSegment(sketch, "E39.right", {"start": v(-42.16, -9.35) * mm, "end": v(-42.16, 3.35) * mm});
            skLineSegment(sketch, "E40.0", {"start": v(5.59, -13.62) * mm, "end": v(-43.69, -13.62) * mm, "construction": true});
            skLineSegment(sketch, "E41.0", {"start": v(8, 2.54) * mm, "end": v(8, -8.54) * mm, "construction": true});
            skLineSegment(sketch, "E42", {"start": v(-19.05, -13.62) * mm, "end": v(-19.05, 11.03) * mm, "construction": true});
            skPoint(sketch, "E42.endSnap0", {"position": v(-19.05, -13.62) * mm});
            skLineSegment(sketch, "E43", {"start": v(8, -3) * mm, "end": v(-32.54, -3) * mm, "construction": true});
            skSolve(sketch);
        }
        {
            var Q0;
            {var subQ0=sQuery(id+"F16.wireOp",EDGE,"E39.top");var subQ1=sQuery(id+"F16.wireOp",EDGE,"E37");var subQ2=makeQuery(id+"F16.imprint","INTERSECT",VERTEX,{"derivedFrom":[subQ1,subQ0]});Q0=makeQuery(id+"F16.imprint","IMPRINT",FACE,{"disambiguationData":[TD([[makeQuery(id+"F16.imprint","IMPRINT",EDGE,{"disambiguationData":[TD([[subQ2,-1.0]])],"derivedFrom":subQ1}),1.0]])]});}
            var Q1;
            {var subQ0=sQuery(id+"F16.wireOp",EDGE,"E39.top");var subQ1=sQuery(id+"F16.wireOp",EDGE,"E37");var subQ2=makeQuery(id+"F16.imprint","INTERSECT",VERTEX,{"derivedFrom":[subQ1,subQ0]});Q1=makeQuery(id+"F16.imprint","IMPRINT",FACE,{"disambiguationData":[TD([[makeQuery(id+"F16.imprint","IMPRINT",EDGE,{"disambiguationData":[TD([[subQ2,1.0]])],"derivedFrom":subQ1}),1.0]])]});}
            var Q2;
            {var subQ0=sQuery(id+"F16.wireOp",EDGE,"E39.bottom");var subQ1=sQuery(id+"F16.wireOp",EDGE,"E38");var subQ2=makeQuery(id+"F16.imprint","INTERSECT",VERTEX,{"derivedFrom":[subQ1,subQ0]});Q2=makeQuery(id+"F16.imprint","IMPRINT",FACE,{"disambiguationData":[TD([[makeQuery(id+"F16.imprint","IMPRINT",EDGE,{"disambiguationData":[TD([[subQ2,1.0]])],"derivedFrom":subQ1}),1.0]])]});}
            var Q3;
            {var subQ0=sQuery(id+"F16.wireOp",EDGE,"E39.bottom");var subQ1=sQuery(id+"F16.wireOp",EDGE,"E38");var subQ2=makeQuery(id+"F16.imprint","INTERSECT",VERTEX,{"derivedFrom":[subQ1,subQ0]});Q3=makeQuery(id+"F16.imprint","IMPRINT",FACE,{"disambiguationData":[TD([[makeQuery(id+"F16.imprint","IMPRINT",EDGE,{"disambiguationData":[TD([[subQ2,-1.0]])],"derivedFrom":subQ1}),1.0]])]});}
            var Q4;
            {var subQ0=sQuery(id+"F16.wireOp",EDGE,"E39.top");var subQ1=sQuery(id+"F16.wireOp",EDGE,"E35");var subQ2=makeQuery(id+"F16.imprint","INTERSECT",VERTEX,{"derivedFrom":[subQ1,subQ0]});Q4=makeQuery(id+"F16.imprint","IMPRINT",FACE,{"disambiguationData":[TD([[makeQuery(id+"F16.imprint","IMPRINT",EDGE,{"disambiguationData":[TD([[subQ2,-1.0]])],"derivedFrom":subQ1}),1.0]])]});}
            var Q5;
            {var subQ0=sQuery(id+"F16.wireOp",EDGE,"E39.top");var subQ1=sQuery(id+"F16.wireOp",EDGE,"E35");var subQ2=makeQuery(id+"F16.imprint","INTERSECT",VERTEX,{"derivedFrom":[subQ1,subQ0]});Q5=makeQuery(id+"F16.imprint","IMPRINT",FACE,{"disambiguationData":[TD([[makeQuery(id+"F16.imprint","IMPRINT",EDGE,{"disambiguationData":[TD([[subQ2,1.0]])],"derivedFrom":subQ1}),1.0]])]});}
            var Q6;
            {var subQ0=sQuery(id+"F16.wireOp",EDGE,"E39.bottom");var subQ1=sQuery(id+"F16.wireOp",EDGE,"E36");var subQ2=makeQuery(id+"F16.imprint","INTERSECT",VERTEX,{"derivedFrom":[subQ1,subQ0]});Q6=makeQuery(id+"F16.imprint","IMPRINT",FACE,{"disambiguationData":[TD([[makeQuery(id+"F16.imprint","IMPRINT",EDGE,{"disambiguationData":[TD([[subQ2,1.0]])],"derivedFrom":subQ1}),1.0]])]});}
            var Q7;
            {var subQ0=sQuery(id+"F16.wireOp",EDGE,"E39.bottom");var subQ1=sQuery(id+"F16.wireOp",EDGE,"E36");var subQ2=makeQuery(id+"F16.imprint","INTERSECT",VERTEX,{"derivedFrom":[subQ1,subQ0]});Q7=makeQuery(id+"F16.imprint","IMPRINT",FACE,{"disambiguationData":[TD([[makeQuery(id+"F16.imprint","IMPRINT",EDGE,{"disambiguationData":[TD([[subQ2,-1.0]])],"derivedFrom":subQ1}),1.0]])]});}
            extrude(context, id + "F17", {"entities" : qUnion([Q0, Q1, Q2, Q3, Q4, Q5, Q6, Q7]), "operationType" : NewBodyOperationType.REMOVE, "endBound" : BoundingType.THROUGH_ALL, "oppositeDirection" : true, "depth" : 25.4 * mm});
        }
        {
            var Q0;
            {var subQ0=sQuery(id+"F0.wireOp",EDGE,"E11");var subQ1=makeQuery(id+"F14.boolean.opBoolean","MERGE",FACE,{"derivedFrom":[makeQuery(id+"F10.boolean.opBoolean","MERGE",FACE,{"derivedFrom":[makeQuery(id+"F4.opBoolean","COPY",FACE,{"derivedFrom":makeQuery(id+"F1.opExtrude","SWEPT_FACE",FACE,{"disambiguationData":[OSD([subQ0])]})}),makeQuery(id+"F10.opExtrude","SWEPT_FACE",FACE,{"disambiguationData":[OSD([subQ0])]})]}),makeQuery(id+"F14.opExtrude","SWEPT_FACE",FACE,{"disambiguationData":[OSD([sQuery(id+"F13.wireOp",EDGE,"E28.0"),sQuery(id+"F13.wireOp",EDGE,"E31.0"),sQuery(id+"F13.wireOp",EDGE,"E32.0")])]})]});Q0=makeQuery(id+"F15.boolean.opBoolean","MERGE",FACE,{"derivedFrom":[subQ1,makeQuery(id+"F15.opPattern","COPY",FACE,{"derivedFrom":subQ1,"instanceName":"1"})]});}
            var sketch = newSketch(context, id + "F18", { "sketchPlane" : qUnion([Q0])});
            skLineSegment(sketch, "E44.bottom", {"start": v(-6.35, -13.62) * mm, "end": v(-31.75, -13.62) * mm});
            skLineSegment(sketch, "E44.top", {"start": v(-6.35, -8.77) * mm, "end": v(-31.75, -8.77) * mm});
            skLineSegment(sketch, "E44.left", {"start": v(-6.35, -13.62) * mm, "end": v(-6.35, -8.77) * mm});
            skLineSegment(sketch, "E44.right", {"start": v(-31.75, -13.62) * mm, "end": v(-31.75, -8.77) * mm});
            skLineSegment(sketch, "E45.bottom", {"start": v(-6.35, 7.62) * mm, "end": v(-31.75, 7.62) * mm});
            skLineSegment(sketch, "E45.top", {"start": v(-6.35, 2.4) * mm, "end": v(-31.75, 2.4) * mm});
            skLineSegment(sketch, "E45.left", {"start": v(-6.35, 7.62) * mm, "end": v(-6.35, 2.4) * mm});
            skLineSegment(sketch, "E45.right", {"start": v(-31.75, 7.62) * mm, "end": v(-31.75, 2.4) * mm});
            skLineSegment(sketch, "E46.bottom", {"start": v(-6.35, -13.62) * mm, "end": v(-12.69, -13.62) * mm});
            skLineSegment(sketch, "E46.top", {"start": v(-6.35, 7.62) * mm, "end": v(-12.69, 7.62) * mm});
            skLineSegment(sketch, "E46.left", {"start": v(-6.35, -13.62) * mm, "end": v(-6.35, 7.62) * mm});
            skLineSegment(sketch, "E46.right", {"start": v(-12.69, -13.62) * mm, "end": v(-12.69, 7.62) * mm});
            skLineSegment(sketch, "E47.bottom", {"start": v(-31.75, -13.62) * mm, "end": v(-25.41, -13.62) * mm});
            skLineSegment(sketch, "E47.top", {"start": v(-31.75, 7.62) * mm, "end": v(-25.41, 7.62) * mm});
            skLineSegment(sketch, "E47.left", {"start": v(-31.75, -13.62) * mm, "end": v(-31.75, 7.62) * mm});
            skLineSegment(sketch, "E47.right", {"start": v(-25.41, -13.62) * mm, "end": v(-25.41, 7.62) * mm});
            skLineSegment(sketch, "E48", {"start": v(-31.75, 7.62) * mm, "end": v(-31.75, 71.12) * mm});
            skLineSegment(sketch, "E49", {"start": v(-6.35, 7.62) * mm, "end": v(-6.35, 71.12) * mm});
            skArc(sketch, "E50", {"start": v(-6.35, 71.12) * mm, "mid": v(-19.05, 83.82) * mm, "end": v(-31.75, 71.12) * mm});
            skPoint(sketch, "E51", {"position": v(-19.05, -13.62) * mm});
            skLineSegment(sketch, "E52", {"start": v(-12.69, -3) * mm, "end": v(-25.41, -3) * mm});
            skLineSegment(sketch, "E53", {"start": v(-19.05, -3) * mm, "end": v(-19.05, -13.62) * mm});
            skSolve(sketch);
        }
        {
            var Q0;
            {var subQ0=sQuery(id+"F18.wireOp",EDGE,"E46.left");var subQ1=sQuery(id+"F18.wireOp",EDGE,"E44.top");var subQ2=makeQuery(id+"F18.imprint","INTERSECT",VERTEX,{"derivedFrom":[subQ1,subQ0]});Q0=makeQuery(id+"F18.imprint","IMPRINT",FACE,{"disambiguationData":[TD([[makeQuery(id+"F18.imprint","IMPRINT",EDGE,{"disambiguationData":[TD([[subQ2,-1.0]])],"derivedFrom":subQ1}),-1.0]])]});}
            var Q1;
            {var subQ5=sQuery(id+"F18.wireOp",EDGE,"E46.top");Q1=makeQuery(id+"F18.imprint","IMPRINT",FACE,{"disambiguationData":[TD([[makeQuery(id+"F18.imprint","IMPRINT",EDGE,{"derivedFrom":subQ5}),-1.0]])]});}
            var Q2;
            {var subQ0=sQuery(id+"F18.wireOp",EDGE,"E45.bottom");Q2=makeQuery(id+"F18.imprint","IMPRINT",FACE,{"disambiguationData":[TD([[makeQuery(id+"F18.imprint","IMPRINT",EDGE,{"derivedFrom":subQ0}),-1.0]])]});}
            var Q3;
            {var subQ5=sQuery(id+"F18.wireOp",EDGE,"E47.top");Q3=makeQuery(id+"F18.imprint","IMPRINT",FACE,{"disambiguationData":[TD([[makeQuery(id+"F18.imprint","IMPRINT",EDGE,{"derivedFrom":subQ5}),-1.0]])]});}
            var Q4;
            {var subQ0=sQuery(id+"F18.wireOp",EDGE,"E47.left");var subQ1=sQuery(id+"F18.wireOp",EDGE,"E44.top");var subQ2=makeQuery(id+"F18.imprint","INTERSECT",VERTEX,{"derivedFrom":[subQ1,subQ0]});Q4=makeQuery(id+"F18.imprint","IMPRINT",FACE,{"disambiguationData":[TD([[makeQuery(id+"F18.imprint","IMPRINT",EDGE,{"disambiguationData":[TD([[subQ2,1.0]])],"derivedFrom":subQ1}),-1.0]])]});}
            var Q5;
            {var subQ5=sQuery(id+"F18.wireOp",EDGE,"E47.bottom");Q5=makeQuery(id+"F18.imprint","IMPRINT",FACE,{"disambiguationData":[TD([[makeQuery(id+"F18.imprint","IMPRINT",EDGE,{"derivedFrom":subQ5}),-1.0]])]});}
            var Q6;
            {var subQ0=sQuery(id+"F18.wireOp",EDGE,"E44.bottom");Q6=makeQuery(id+"F18.imprint","IMPRINT",FACE,{"disambiguationData":[TD([[makeQuery(id+"F18.imprint","IMPRINT",EDGE,{"derivedFrom":subQ0}),-1.0]])]});}
            var Q7;
            {var subQ5=sQuery(id+"F18.wireOp",EDGE,"E46.bottom");Q7=makeQuery(id+"F18.imprint","IMPRINT",FACE,{"disambiguationData":[TD([[makeQuery(id+"F18.imprint","IMPRINT",EDGE,{"derivedFrom":subQ5}),-1.0]])]});}
            var Q8;
            Q8=makeQuery(id+"F18.imprint","IMPRINT",FACE,{"disambiguationData":[TD([[makeQuery(id+"F18.imprint","IMPRINT",EDGE,{"derivedFrom":sQuery(id+"F18.wireOp",EDGE,"E45.bottom")}),1.0]])]});
            var Q9;
            {var subQ0=sQuery(id+"F2.wireOp",EDGE,"E13.bottom");var subQ1=makeQuery(id+"F14.boolean.opBoolean","MERGE",FACE,{"derivedFrom":[makeQuery(id+"F10.boolean.opBoolean","MERGE",FACE,{"derivedFrom":[makeQuery(id+"F3.opExtrude","SWEPT_FACE",FACE,{"disambiguationData":[OSD([subQ0])]}),makeQuery(id+"F10.opExtrude","SWEPT_FACE",FACE,{"disambiguationData":[OSD([subQ0])]})]}),makeQuery(id+"F14.opExtrude","SWEPT_FACE",FACE,{"disambiguationData":[OSD([sQuery(id+"F13.wireOp",EDGE,"E29.0"),sQuery(id+"F13.wireOp",EDGE,"E30.0"),sQuery(id+"F13.wireOp",EDGE,"E34.0")])]})]});Q9=makeQuery(id+"F15.boolean.opBoolean","MERGE",FACE,{"derivedFrom":[subQ1,makeQuery(id+"F15.opPattern","COPY",FACE,{"derivedFrom":subQ1,"instanceName":"1"})]});}
            extrude(context, id + "F19", {"entities" : qUnion([Q0, Q1, Q2, Q3, Q4, Q5, Q6, Q7, Q8]), "operationType" : NewBodyOperationType.ADD, "depth" : 3.17 * mm, "hasSecondDirection" : true, "secondDirectionBound" : SecondDirectionBoundingType.UP_TO_SURFACE, "secondDirectionOppositeDirection" : true, "secondDirectionBoundEntityFace" : qUnion([Q9]), "secondDirectionDepth" : 25.4 * mm});
        }
        {
            var Q0;
            Q0=makeQuery(id+"F19.opExtrude","CAP_FACE",FACE,{"disambiguationData":[OSD([sQuery(id+"F18.wireOp",EDGE,"E44.bottom"),sQuery(id+"F18.wireOp",EDGE,"E44.top"),sQuery(id+"F18.wireOp",EDGE,"E45.top"),sQuery(id+"F18.wireOp",EDGE,"E46.bottom"),sQuery(id+"F18.wireOp",EDGE,"E46.left"),sQuery(id+"F18.wireOp",EDGE,"E46.right"),sQuery(id+"F18.wireOp",EDGE,"E47.bottom"),sQuery(id+"F18.wireOp",EDGE,"E47.left"),sQuery(id+"F18.wireOp",EDGE,"E47.right"),sQuery(id+"F18.wireOp",EDGE,"E48"),sQuery(id+"F18.wireOp",EDGE,"E49"),sQuery(id+"F18.wireOp",EDGE,"E50")])],"isStart":false});
            var sketch = newSketch(context, id + "F20", { "sketchPlane" : qUnion([Q0])});
            skCircle(sketch, "E54", {"center": v(-14.29, 72.26) * mm, "radius": 1.9 * mm});
            skCircle(sketch, "E55", {"center": v(-23.81, 72.26) * mm, "radius": 1.9 * mm});
            skLineSegment(sketch, "E56", {"start": v(-19.05, 2.4) * mm, "end": v(-19.05, 72.26) * mm});
            skLineSegment(sketch, "E57", {"start": v(-14.29, 72.26) * mm, "end": v(-23.81, 72.26) * mm});
            skSolve(sketch);
        }
        {
            var Q0;
            Q0 = qSketchRegion(id + "F20", true);
            extrude(context, id + "F21", {"entities" : qUnion([Q0]), "operationType" : NewBodyOperationType.REMOVE, "endBound" : BoundingType.THROUGH_ALL, "oppositeDirection" : true, "depth" : 25.4 * mm});
        }
        {
            var Q0;
            Q0=makeQuery(id+"F19.opExtrude","CAP_FACE",FACE,{"disambiguationData":[OSD([sQuery(id+"F18.wireOp",EDGE,"E44.bottom"),sQuery(id+"F18.wireOp",EDGE,"E44.top"),sQuery(id+"F18.wireOp",EDGE,"E45.top"),sQuery(id+"F18.wireOp",EDGE,"E46.bottom"),sQuery(id+"F18.wireOp",EDGE,"E46.left"),sQuery(id+"F18.wireOp",EDGE,"E46.right"),sQuery(id+"F18.wireOp",EDGE,"E47.bottom"),sQuery(id+"F18.wireOp",EDGE,"E47.left"),sQuery(id+"F18.wireOp",EDGE,"E47.right"),sQuery(id+"F18.wireOp",EDGE,"E48"),sQuery(id+"F18.wireOp",EDGE,"E49"),sQuery(id+"F18.wireOp",EDGE,"E50")])],"isStart":false});
            var sketch = newSketch(context, id + "F22", { "sketchPlane" : qUnion([Q0])});
            skLineSegment(sketch, "E58.bottom", {"start": v(-15.51, 11.72) * mm, "end": v(-22.53, 11.72) * mm});
            skLineSegment(sketch, "E58.top", {"start": v(-15.51, 48.85) * mm, "end": v(-22.53, 48.85) * mm});
            skLineSegment(sketch, "E58.left", {"start": v(-15.51, 11.72) * mm, "end": v(-15.51, 48.85) * mm});
            skLineSegment(sketch, "E58.right", {"start": v(-22.53, 11.72) * mm, "end": v(-22.53, 48.85) * mm});
            skSolve(sketch);
        }
        {
            var Q0;
            Q0 = qSketchRegion(id + "F22", true);
            extrude(context, id + "F23", {"entities" : qUnion([Q0]), "operationType" : NewBodyOperationType.REMOVE, "endBound" : BoundingType.THROUGH_ALL, "oppositeDirection" : true, "depth" : 25.4 * mm});
        }
        {
            var Q0;
            Q0=makeQuery(id+"F19.opExtrude","CAP_VERTEX",VERTEX,{"disambiguationData":[OSD([sQuery(id+"F18.wireOp",EDGE,"E49"),sQuery(id+"F18.wireOp",EDGE,"E50")])],"isStart":false});
            var Q1;
            Q1=makeQuery(id+"F19.opExtrude","CAP_VERTEX",VERTEX,{"disambiguationData":[OSD([sQuery(id+"F18.wireOp",EDGE,"E46.left"),sQuery(id+"F18.wireOp",EDGE,"E49"),sQuery(id+"F18.wireOp",EDGE,"E50")])],"isStart":true});
            var Q2;
            Q2=makeQuery(id+"F19.opExtrude","CAP_VERTEX",VERTEX,{"disambiguationData":[OSD([sQuery(id+"F18.wireOp",EDGE,"E48"),sQuery(id+"F18.wireOp",EDGE,"E50")])],"isStart":false});
            cPlane(context, id + "F24", {"entities" : qUnion([Q0, Q1, Q2]), "cplaneType" : CPlaneType.THREE_POINT, "offset" : 152.4 * mm, "width" : 152.4 * mm, "height" : 152.4 * mm});
        }
        {
            var Q0;
            Q0=qCreatedBy(id+"F24.planeOp",FACE);
            var sketch = newSketch(context, id + "F25", { "sketchPlane" : qUnion([Q0])});
            skLineSegment(sketch, "E59.0", {"start": v(-31.75, 2.41) * mm, "end": v(-6.35, 2.41) * mm, "construction": true});
            skLineSegment(sketch, "E60", {"start": v(-19.05, 2.41) * mm, "end": v(-19.05, 8.76) * mm, "construction": true});
            skLineSegment(sketch, "E61", {"start": v(31.75, 8.76) * mm, "end": v(-69.85, 8.76) * mm});
            skLineSegment(sketch, "E62", {"start": v(-69.85, 8.76) * mm, "end": v(-82.55, 34.16) * mm});
            skLineSegment(sketch, "E63", {"start": v(-82.55, 34.16) * mm, "end": v(44.45, 34.16) * mm});
            skLineSegment(sketch, "E64", {"start": v(44.45, 34.16) * mm, "end": v(31.75, 8.76) * mm});
            skLineSegment(sketch, "E65", {"start": v(-19.05, 8.76) * mm, "end": v(-19.05, 34.16) * mm});
            skSolve(sketch);
        }
        {
            var Q0;
            Q0 = qSketchRegion(id + "F25", true);
            var Q1;
            {var subQ0=sQuery(id+"F25.wireOp",EDGE,"E62");Q1=makeQuery(id+"F25.imprint","IMPRINT",FACE,{"disambiguationData":[TD([[makeQuery(id+"F25.imprint","IMPRINT",EDGE,{"derivedFrom":subQ0}),-1.0]])]});}
            extrude(context, id + "F26", {"entities" : qUnion([Q0, Q1]), "endBound" : BoundingType.SYMMETRIC, "depth" : 38.1 * mm});
        }
        {
            var Q0;
            Q0=makeQuery(id+"F26.opExtrude","SWEPT_FACE",FACE,{"disambiguationData":[OSD([sQuery(id+"F25.wireOp",EDGE,"E63")])]});
            var sketch = newSketch(context, id + "F27", { "sketchPlane" : qUnion([Q0])});
            skLineSegment(sketch, "E66.bottom", {"start": v(31.75, 52.07) * mm, "end": v(-69.85, 52.07) * mm});
            skLineSegment(sketch, "E66.top", {"start": v(31.75, 90.17) * mm, "end": v(-69.85, 90.17) * mm});
            skLineSegment(sketch, "E66.left", {"start": v(31.75, 52.07) * mm, "end": v(31.75, 90.17) * mm});
            skLineSegment(sketch, "E66.right", {"start": v(-69.85, 52.07) * mm, "end": v(-69.85, 90.17) * mm});
            skLineSegment(sketch, "E67.bottom", {"start": v(16.66, 42.54) * mm, "end": v(-54.76, 42.54) * mm});
            skLineSegment(sketch, "E67.top", {"start": v(16.66, 99.7) * mm, "end": v(-54.76, 99.7) * mm});
            skLineSegment(sketch, "E67.left", {"start": v(16.66, 42.54) * mm, "end": v(16.66, 99.7) * mm});
            skLineSegment(sketch, "E67.right", {"start": v(-54.76, 42.54) * mm, "end": v(-54.76, 99.7) * mm});
            skLineSegment(sketch, "E68", {"start": v(-69.85, 52.07) * mm, "end": v(31.75, 90.17) * mm, "construction": true});
            skPoint(sketch, "E69", {"position": v(-19.05, 52.07) * mm});
            skLineSegment(sketch, "E70", {"start": v(16.66, 42.54) * mm, "end": v(-54.76, 99.7) * mm});
            skPoint(sketch, "E71", {"position": v(-19.05, 71.12) * mm});
            skSolve(sketch);
        }
        {
            var Q0;
            Q0 = qSketchRegion(id + "F27", true);
            extrude(context, id + "F28", {"entities" : qUnion([Q0]), "operationType" : NewBodyOperationType.ADD, "depth" : 6.35 * mm});
        }
        {
            var Q0;
            Q0=makeQuery(id+"F28.opExtrude","CAP_FACE",FACE,{"disambiguationData":[OSD([sQuery(id+"F27.wireOp",EDGE,"E66.bottom"),sQuery(id+"F27.wireOp",EDGE,"E66.top"),sQuery(id+"F27.wireOp",EDGE,"E66.left"),sQuery(id+"F27.wireOp",EDGE,"E66.right"),sQuery(id+"F27.wireOp",EDGE,"E67.bottom"),sQuery(id+"F27.wireOp",EDGE,"E67.top"),sQuery(id+"F27.wireOp",EDGE,"E67.left"),sQuery(id+"F27.wireOp",EDGE,"E67.right")])],"isStart":false});
            var sketch = newSketch(context, id + "F29", { "sketchPlane" : qUnion([Q0])});
            skText(sketch, "E72", { "text": "X", "fontName": "OpenSans-Regular.ttf"});
            const initialGuessF29  = {"E72": [-0.03028, 0.04707, 1, 0, 0.01526]};
            skSetInitialGuess(sketch, initialGuessF29);
            skSolve(sketch);
        }
        {
            var Q0;
            Q0 = qSketchRegion(id + "F29", true);
            extrude(context, id + "F30", {"entities" : qUnion([Q0]), "operationType" : NewBodyOperationType.REMOVE, "oppositeDirection" : true, "depth" : 3.17 * mm});
        }
        {
            var Q0;
            Q0=qCreatedBy(id+"F24.planeOp",FACE);
            cPlane(context, id + "F31", {"entities" : qUnion([Q0]), "cplaneType" : CPlaneType.OFFSET, "offset" : 50.8 * mm, "width" : 152.4 * mm, "height" : 152.4 * mm});
        }
        {
            var Q0;
            Q0=qCreatedBy(id+"F31.planeOp",FACE);
            var sketch = newSketch(context, id + "F32", { "sketchPlane" : qUnion([Q0])});
            skLineSegment(sketch, "E73.bottom", {"start": v(457.2, 76.2) * mm, "end": v(-457.2, 76.2) * mm});
            skLineSegment(sketch, "E73.top", {"start": v(457.2, -76.2) * mm, "end": v(-457.2, -76.2) * mm});
            skLineSegment(sketch, "E73.left", {"start": v(457.2, 76.2) * mm, "end": v(457.2, -76.2) * mm});
            skLineSegment(sketch, "E73.right", {"start": v(-457.2, 76.2) * mm, "end": v(-457.2, -76.2) * mm});
            skPoint(sketch, "E73.middle", {"position": v(0, 0) * mm});
            skLineSegment(sketch, "E74.bottom", {"start": v(355.6, 6.35) * mm, "end": v(-355.6, 6.35) * mm});
            skLineSegment(sketch, "E74.top", {"start": v(355.6, -6.35) * mm, "end": v(-355.6, -6.35) * mm});
            skLineSegment(sketch, "E74.left", {"start": v(355.6, 6.35) * mm, "end": v(355.6, -6.35) * mm, "construction": true});
            skLineSegment(sketch, "E74.right", {"start": v(-355.6, 6.35) * mm, "end": v(-355.6, -6.35) * mm, "construction": true});
            skArc(sketch, "E75", {"start": v(-355.6, 6.35) * mm, "mid": v(-361.95, 0) * mm, "end": v(-355.6, -6.35) * mm});
            skArc(sketch, "E76", {"start": v(355.6, 6.35) * mm, "mid": v(361.95, 0) * mm, "end": v(355.6, -6.35) * mm});
            skLineSegment(sketch, "E77.bottom", {"start": v(-390.9, 15.5) * mm, "end": v(-421.9, 15.5) * mm, "construction": true});
            skLineSegment(sketch, "E77.top", {"start": v(-390.9, -15.5) * mm, "end": v(-421.9, -15.5) * mm, "construction": true});
            skLineSegment(sketch, "E77.left", {"start": v(-390.9, 15.5) * mm, "end": v(-390.9, -15.5) * mm, "construction": true});
            skLineSegment(sketch, "E77.right", {"start": v(-421.9, 15.5) * mm, "end": v(-421.9, -15.5) * mm, "construction": true});
            skPoint(sketch, "E77.middle", {"position": v(-406.4, 0) * mm});
            skLineSegment(sketch, "E78", {"start": v(-406.4, 0) * mm, "end": v(-355.6, 0) * mm, "construction": true});
            skCircle(sketch, "E79", {"center": v(-390.9, 15.5) * mm, "radius": 1.25 * mm});
            skCircle(sketch, "E80", {"center": v(-421.9, -15.5) * mm, "radius": 1.25 * mm});
            skCircle(sketch, "E81", {"center": v(-390.9, -15.5) * mm, "radius": 1.25 * mm});
            skCircle(sketch, "E82", {"center": v(-421.9, 15.5) * mm, "radius": 1.25 * mm});
            skLineSegment(sketch, "E83", {"start": v(355.6, 0) * mm, "end": v(381, 0) * mm, "construction": true});
            skCircle(sketch, "E84", {"center": v(381, 0) * mm, "radius": 2.38 * mm});
            skLineSegment(sketch, "E85.bottom", {"start": v(406.4, 25.4) * mm, "end": v(355.6, 25.4) * mm, "construction": true});
            skLineSegment(sketch, "E85.top", {"start": v(406.4, -25.4) * mm, "end": v(355.6, -25.4) * mm, "construction": true});
            skLineSegment(sketch, "E85.left", {"start": v(406.4, 25.4) * mm, "end": v(406.4, -25.4) * mm, "construction": true});
            skLineSegment(sketch, "E85.right", {"start": v(355.6, 25.4) * mm, "end": v(355.6, -25.4) * mm, "construction": true});
            skCircle(sketch, "E86", {"center": v(355.6, 25.4) * mm, "radius": 1.25 * mm});
            skCircle(sketch, "E87", {"center": v(406.4, 25.4) * mm, "radius": 1.25 * mm});
            skCircle(sketch, "E88", {"center": v(355.6, -25.4) * mm, "radius": 1.25 * mm});
            skCircle(sketch, "E89", {"center": v(406.4, -25.4) * mm, "radius": 1.25 * mm});
            skSolve(sketch);
        }
        {
            var Q0;
            Q0=makeQuery(id+"F32.imprint","IMPRINT",FACE,{"disambiguationData":[TD([[makeQuery(id+"F32.imprint","IMPRINT",EDGE,{"derivedFrom":sQuery(id+"F32.wireOp",EDGE,"E73.bottom")}),1.0]])]});
            extrude(context, id + "F33", {"entities" : qUnion([Q0]), "oppositeDirection" : true, "depth" : 17.78 * mm});
        }
        {
            var Q0;
            Q0=makeQuery(id+"F33.opExtrude","CAP_FACE",FACE,{"disambiguationData":[OSD([sQuery(id+"F32.wireOp",EDGE,"E73.bottom"),sQuery(id+"F32.wireOp",EDGE,"E73.top"),sQuery(id+"F32.wireOp",EDGE,"E73.left"),sQuery(id+"F32.wireOp",EDGE,"E73.right"),sQuery(id+"F32.wireOp",EDGE,"E74.bottom"),sQuery(id+"F32.wireOp",EDGE,"E74.top"),sQuery(id+"F32.wireOp",EDGE,"E75"),sQuery(id+"F32.wireOp",EDGE,"E76"),sQuery(id+"F32.wireOp",EDGE,"E79"),sQuery(id+"F32.wireOp",EDGE,"E80"),sQuery(id+"F32.wireOp",EDGE,"E81"),sQuery(id+"F32.wireOp",EDGE,"E82")])],"isStart":true});
            var sketch = newSketch(context, id + "F34", { "sketchPlane" : qUnion([Q0])});
            skCircle(sketch, "E90", {"center": v(-421.9, 15.5) * mm, "radius": 1.46 * mm});
            skCircle(sketch, "E91", {"center": v(-421.9, 15.5) * mm, "radius": 3.18 * mm});
            skCircle(sketch, "E92", {"center": v(-390.9, 15.5) * mm, "radius": 1.46 * mm});
            skCircle(sketch, "E93", {"center": v(-390.9, 15.5) * mm, "radius": 3.18 * mm});
            skCircle(sketch, "E94", {"center": v(-390.9, -15.5) * mm, "radius": 3.18 * mm});
            skCircle(sketch, "E95", {"center": v(-390.9, -15.5) * mm, "radius": 1.46 * mm});
            skCircle(sketch, "E96", {"center": v(-421.9, -15.5) * mm, "radius": 3.18 * mm});
            skCircle(sketch, "E97", {"center": v(-421.9, -15.5) * mm, "radius": 1.46 * mm});
            skCircle(sketch, "E98", {"center": v(406.4, 25.4) * mm, "radius": 1.46 * mm});
            skCircle(sketch, "E99", {"center": v(406.4, 25.4) * mm, "radius": 3.18 * mm});
            skCircle(sketch, "E100", {"center": v(355.6, 25.4) * mm, "radius": 1.46 * mm});
            skCircle(sketch, "E101", {"center": v(355.6, 25.4) * mm, "radius": 3.18 * mm});
            skCircle(sketch, "E102", {"center": v(355.6, -25.4) * mm, "radius": 3.18 * mm});
            skCircle(sketch, "E103", {"center": v(355.6, -25.4) * mm, "radius": 1.46 * mm});
            skCircle(sketch, "E104", {"center": v(406.4, -25.4) * mm, "radius": 3.18 * mm});
            skCircle(sketch, "E105", {"center": v(406.4, -25.4) * mm, "radius": 1.46 * mm});
            skSolve(sketch);
        }
        {
            var Q0;
            Q0 = qSketchRegion(id + "F34", true);
            extrude(context, id + "F35", {"entities" : qUnion([Q0]), "depth" : 50.8 * mm});
        }
        {
            var Q0;
            Q0=makeQuery(id+"F35.opExtrude","CAP_FACE",FACE,{"disambiguationData":[OSD([sQuery(id+"F34.wireOp",EDGE,"E100"),sQuery(id+"F34.wireOp",EDGE,"E101")])],"isStart":false});
            var sketch = newSketch(context, id + "F36", { "sketchPlane" : qUnion([Q0])});
            skLineSegment(sketch, "E106.bottom", {"start": v(411.29, 36.64) * mm, "end": v(350.71, 36.64) * mm});
            skLineSegment(sketch, "E106.top", {"start": v(411.29, -36.64) * mm, "end": v(350.71, -36.64) * mm});
            skLineSegment(sketch, "E106.left", {"start": v(417.64, 30.29) * mm, "end": v(417.64, -30.29) * mm});
            skLineSegment(sketch, "E106.right", {"start": v(344.36, 30.29) * mm, "end": v(344.36, -30.29) * mm});
            skPoint(sketch, "E106.middle", {"position": v(381, 0) * mm});
            skPoint(sketch, "E107.visualSharp", {"position": v(344.36, 36.64) * mm});
            skArc(sketch, "E107.filletArc", {"start": v(350.71, 36.64) * mm, "mid": v(346.22, 34.78) * mm, "end": v(344.36, 30.29) * mm});
            skPoint(sketch, "E108.visualSharp", {"position": v(417.64, 36.64) * mm});
            skArc(sketch, "E108.filletArc", {"start": v(417.64, 30.29) * mm, "mid": v(415.78, 34.78) * mm, "end": v(411.29, 36.64) * mm});
            skPoint(sketch, "E109.visualSharp", {"position": v(417.64, -36.64) * mm});
            skArc(sketch, "E109.filletArc", {"start": v(411.29, -36.64) * mm, "mid": v(415.78, -34.78) * mm, "end": v(417.64, -30.29) * mm});
            skPoint(sketch, "E110.visualSharp", {"position": v(344.36, -36.64) * mm});
            skArc(sketch, "E110.filletArc", {"start": v(344.36, -30.29) * mm, "mid": v(346.22, -34.78) * mm, "end": v(350.71, -36.64) * mm});
            skCircle(sketch, "E111", {"center": v(381, 0) * mm, "radius": 2.38 * mm});
            skLineSegment(sketch, "E112", {"start": v(367.24, 28.58) * mm, "end": v(394.76, 28.58) * mm});
            skLineSegment(sketch, "E113", {"start": v(395.88, 26.7) * mm, "end": v(387.07, 10.2) * mm});
            skLineSegment(sketch, "E114", {"start": v(385.95, 9.53) * mm, "end": v(376.05, 9.53) * mm});
            skLineSegment(sketch, "E115", {"start": v(374.93, 10.2) * mm, "end": v(366.12, 26.7) * mm});
            skLineSegment(sketch, "E116", {"start": v(352.42, 13.76) * mm, "end": v(352.42, -13.76) * mm});
            skLineSegment(sketch, "E117", {"start": v(354.3, -14.88) * mm, "end": v(370.8, -6.07) * mm});
            skLineSegment(sketch, "E118", {"start": v(371.47, -4.95) * mm, "end": v(371.47, 4.95) * mm});
            skLineSegment(sketch, "E119", {"start": v(370.8, 6.07) * mm, "end": v(354.3, 14.88) * mm});
            skLineSegment(sketch, "E120", {"start": v(367.24, -28.58) * mm, "end": v(394.76, -28.58) * mm});
            skLineSegment(sketch, "E121", {"start": v(395.88, -26.7) * mm, "end": v(387.07, -10.2) * mm});
            skLineSegment(sketch, "E122", {"start": v(385.95, -9.53) * mm, "end": v(376.05, -9.53) * mm});
            skLineSegment(sketch, "E123", {"start": v(374.93, -10.2) * mm, "end": v(366.12, -26.7) * mm});
            skLineSegment(sketch, "E124", {"start": v(407.7, 14.88) * mm, "end": v(391.2, 6.07) * mm});
            skLineSegment(sketch, "E125", {"start": v(390.52, 4.95) * mm, "end": v(390.52, -4.95) * mm});
            skLineSegment(sketch, "E126", {"start": v(391.2, -6.07) * mm, "end": v(407.7, -14.88) * mm});
            skLineSegment(sketch, "E127", {"start": v(409.57, -13.76) * mm, "end": v(409.57, 13.76) * mm});
            skLineSegment(sketch, "E128", {"start": v(371.47, 5.72) * mm, "end": v(371.47, 9.53) * mm, "construction": true});
            skLineSegment(sketch, "E129", {"start": v(371.47, 9.53) * mm, "end": v(375.28, 9.53) * mm, "construction": true});
            skLineSegment(sketch, "E130", {"start": v(386.71, 9.53) * mm, "end": v(390.52, 9.53) * mm, "construction": true});
            skLineSegment(sketch, "E131", {"start": v(390.52, 9.53) * mm, "end": v(390.52, 5.72) * mm, "construction": true});
            skLineSegment(sketch, "E132", {"start": v(390.52, -5.71) * mm, "end": v(390.52, -9.53) * mm, "construction": true});
            skLineSegment(sketch, "E133", {"start": v(390.52, -9.53) * mm, "end": v(386.71, -9.53) * mm, "construction": true});
            skLineSegment(sketch, "E134", {"start": v(375.28, -9.53) * mm, "end": v(371.47, -9.53) * mm, "construction": true});
            skLineSegment(sketch, "E135", {"start": v(371.47, -9.53) * mm, "end": v(371.47, -5.71) * mm, "construction": true});
            skLineSegment(sketch, "E136", {"start": v(352.42, 0) * mm, "end": v(371.47, 0) * mm, "construction": true});
            skLineSegment(sketch, "E137", {"start": v(381, -9.53) * mm, "end": v(381, -28.58) * mm, "construction": true});
            skLineSegment(sketch, "E138", {"start": v(390.52, 0) * mm, "end": v(409.57, 0) * mm, "construction": true});
            skLineSegment(sketch, "E139", {"start": v(381, 9.53) * mm, "end": v(381, 28.58) * mm, "construction": true});
            skPoint(sketch, "E139.endSnap0", {"position": v(381, 28.58) * mm});
            skLineSegment(sketch, "E140", {"start": v(371.47, 9.53) * mm, "end": v(390.52, -9.53) * mm, "construction": true});
            skLineSegment(sketch, "E141", {"start": v(390.52, 9.53) * mm, "end": v(371.47, -9.53) * mm, "construction": true});
            skPoint(sketch, "E142.visualSharp", {"position": v(352.42, 15.88) * mm});
            skArc(sketch, "E142.filletArc", {"start": v(354.3, 14.88) * mm, "mid": v(353.04, 14.85) * mm, "end": v(352.42, 13.76) * mm});
            skPoint(sketch, "E143.visualSharp", {"position": v(352.42, -15.88) * mm});
            skArc(sketch, "E143.filletArc", {"start": v(352.42, -13.76) * mm, "mid": v(353.04, -14.85) * mm, "end": v(354.3, -14.88) * mm});
            skPoint(sketch, "E144.visualSharp", {"position": v(371.47, -5.72) * mm});
            skArc(sketch, "E144.filletArc", {"start": v(370.8, -6.07) * mm, "mid": v(371.3, -5.6) * mm, "end": v(371.47, -4.95) * mm});
            skPoint(sketch, "E145.visualSharp", {"position": v(371.47, 5.72) * mm});
            skArc(sketch, "E145.filletArc", {"start": v(371.47, 4.95) * mm, "mid": v(371.3, 5.6) * mm, "end": v(370.8, 6.07) * mm});
            skPoint(sketch, "E146.visualSharp", {"position": v(365.12, -28.58) * mm});
            skArc(sketch, "E146.filletArc", {"start": v(366.12, -26.7) * mm, "mid": v(366.15, -27.96) * mm, "end": v(367.24, -28.58) * mm});
            skPoint(sketch, "E147.visualSharp", {"position": v(375.28, -9.53) * mm});
            skArc(sketch, "E147.filletArc", {"start": v(376.05, -9.53) * mm, "mid": v(375.4, -9.7) * mm, "end": v(374.93, -10.2) * mm});
            skPoint(sketch, "E148.visualSharp", {"position": v(386.71, -9.53) * mm});
            skArc(sketch, "E148.filletArc", {"start": v(387.07, -10.2) * mm, "mid": v(386.6, -9.7) * mm, "end": v(385.95, -9.53) * mm});
            skPoint(sketch, "E149.visualSharp", {"position": v(396.87, -28.58) * mm});
            skArc(sketch, "E149.filletArc", {"start": v(394.76, -28.58) * mm, "mid": v(395.85, -27.96) * mm, "end": v(395.88, -26.7) * mm});
            skPoint(sketch, "E150.visualSharp", {"position": v(409.57, -15.87) * mm});
            skArc(sketch, "E150.filletArc", {"start": v(407.7, -14.88) * mm, "mid": v(408.96, -14.85) * mm, "end": v(409.57, -13.76) * mm});
            skPoint(sketch, "E151.visualSharp", {"position": v(390.52, -5.71) * mm});
            skArc(sketch, "E151.filletArc", {"start": v(390.52, -4.95) * mm, "mid": v(390.7, -5.6) * mm, "end": v(391.2, -6.07) * mm});
            skPoint(sketch, "E152.visualSharp", {"position": v(390.52, 5.71) * mm});
            skArc(sketch, "E152.filletArc", {"start": v(391.2, 6.07) * mm, "mid": v(390.7, 5.6) * mm, "end": v(390.52, 4.95) * mm});
            skPoint(sketch, "E153.visualSharp", {"position": v(409.57, 15.87) * mm});
            skArc(sketch, "E153.filletArc", {"start": v(409.57, 13.76) * mm, "mid": v(408.96, 14.85) * mm, "end": v(407.7, 14.88) * mm});
            skPoint(sketch, "E154.visualSharp", {"position": v(386.71, 9.53) * mm});
            skArc(sketch, "E154.filletArc", {"start": v(385.95, 9.53) * mm, "mid": v(386.6, 9.7) * mm, "end": v(387.07, 10.2) * mm});
            skPoint(sketch, "E155.visualSharp", {"position": v(375.28, 9.53) * mm});
            skArc(sketch, "E155.filletArc", {"start": v(374.93, 10.2) * mm, "mid": v(375.4, 9.7) * mm, "end": v(376.05, 9.53) * mm});
            skPoint(sketch, "E156.visualSharp", {"position": v(365.12, 28.58) * mm});
            skArc(sketch, "E156.filletArc", {"start": v(367.24, 28.58) * mm, "mid": v(366.15, 27.96) * mm, "end": v(366.12, 26.7) * mm});
            skPoint(sketch, "E157.visualSharp", {"position": v(396.87, 28.58) * mm});
            skArc(sketch, "E157.filletArc", {"start": v(395.88, 26.7) * mm, "mid": v(395.85, 27.96) * mm, "end": v(394.76, 28.58) * mm});
            skCircle(sketch, "E158", {"center": v(355.6, 25.4) * mm, "radius": 1.46 * mm});
            skCircle(sketch, "E159", {"center": v(406.4, 25.4) * mm, "radius": 1.46 * mm});
            skCircle(sketch, "E160", {"center": v(355.6, -25.4) * mm, "radius": 1.46 * mm});
            skCircle(sketch, "E161", {"center": v(406.4, -25.4) * mm, "radius": 1.46 * mm});
            skSolve(sketch);
        }
        {
            var Q0;
            Q0 = qSketchRegion(id + "F36", true);
            extrude(context, id + "F37", {"entities" : qUnion([Q0]), "depth" : 6.35 * mm});
        }
    });
